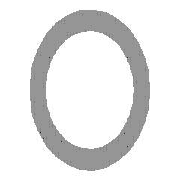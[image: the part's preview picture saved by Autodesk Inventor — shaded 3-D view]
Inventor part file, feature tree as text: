
AUTODESK INVENTOR PART (.ipt)
format: ipt  version: 2021 (Build 250183000, 183)  size: 257,536 bytes
history: native  units: mm (DEFAULTED — no unit token found)
features: other x11, plane x2, sketch x2, sweep x1
ambient origin geometry x8: Origin, YZ Plane, XZ Plane, XY Plane, X Axis, Y Axis, Z Axis, Center Point
bodies: Solid1 (feature_tree)
feature tree (16):
  parser-record x1  (decoder bookkeeping rows leaked as tree rows — omitted from the tree; the rows remain in map.json)
  other  "Driven Length"
  other  "Plano inicial"
  other  "Plano final"
  other  "Trayectoria de barrido"
  plane  "Plano de trabajo de orientación"
  sweep  "Cuerpo"
  sketch  "Sketch3"  dims[d0=26.67mm d1=2.8702mm]
  plane  "Work Plane3"
  sketch  "Sketch4"  dims[d4=-0.0mm d5=545.585311mm d6=90.0deg d7=545.585311mm d8=0.0mm d9=0.0mm d26=10.0mm d31=10.0mm d172=5.0mm d173=0.0mm d174=5.0mm d175=0.0mm]
  other  "Sup118"
  other  "Sup119"
  other  "Sólido40"
  other  "Sup117"
  other  "Superficie de contorno77"
  other  "Superficie de contorno78"
